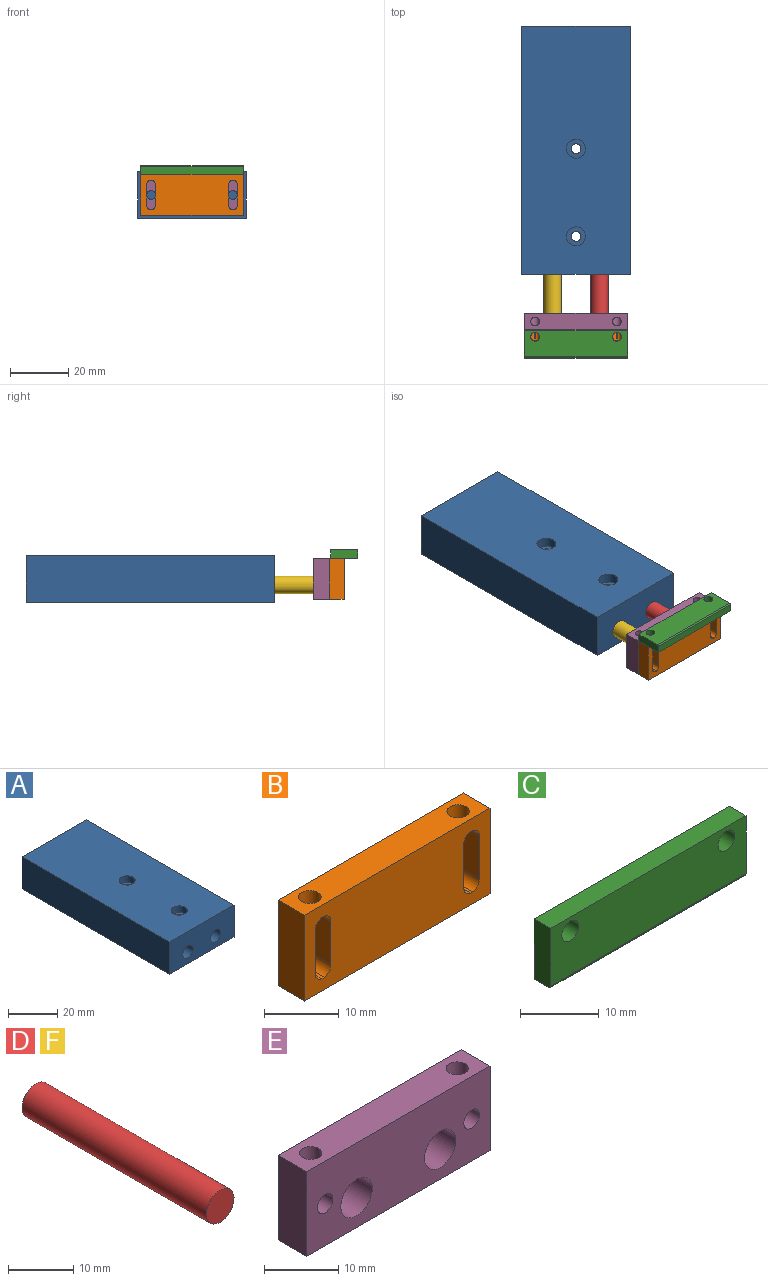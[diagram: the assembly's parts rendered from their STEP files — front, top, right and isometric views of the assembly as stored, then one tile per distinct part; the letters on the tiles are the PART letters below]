
ASSEMBLY  parts=6 mates=8
PART A: 16 faces, bbox 37x85x16 mm
  f0: plane 37x16mm, normal (0,-1,0), area 535.5mm2, adj f1,f3,f4,f5,f6,f8
  f1: plane 85x16mm, normal (1,0,0), area 1360mm2, adj f0,f2,f4,f5
  f2: plane 37x16mm, normal (0,1,0), area 592mm2, adj f1,f3,f4,f5
  f3: plane 85x16mm, normal (-1,0,0), area 1360mm2, adj f0,f2,f4,f5
  f4: plane 85x37mm, normal (0,0,1), area 3078.6mm2, adj f0,f1,f2,f3,f12,f15
  f5: plane 85x37mm, normal (0,0,-1), area 3126.8mm2, adj f0,f1,f2,f3,f10,f13
  f6: cylinder r=3mm len=80mm, axis (0,-1,0), area 1508mm2, adj f0,f7
  f7: plane 6x6mm, normal (0,-1,0), area 28.3mm2, adj f6
  f8: cylinder r=3mm len=80mm, axis (0,-1,0), area 1508mm2, adj f0,f9
  f9: plane 6x6mm, normal (0,-1,0), area 28.3mm2, adj f8
  f10: cylinder r=1.7mm len=12.7mm, axis (0,0,1), area 135.7mm2, adj f5,f11
  f11: plane 6.5x6.5mm, normal (0,0,1), area 24.1mm2, adj f10,f12
  f12: cylinder r=3.25mm len=6.5mm, axis (0,0,1), area 67.4mm2, adj f4,f11
  f13: cylinder r=1.7mm len=12.7mm, axis (0,0,1), area 135.7mm2, adj f5,f14
  f14: plane 6.5x6.5mm, normal (0,0,1), area 24.1mm2, adj f13,f15
  f15: cylinder r=3.25mm len=6.5mm, axis (0,0,1), area 67.4mm2, adj f4,f14
PART B: 30 faces, bbox 35x5x14 mm
  f0: plane 35x5mm, normal (0,0,1), area 160.9mm2, adj f10,f11,f12,f13,f28,f29
  f1: cylinder r=1.5mm len=2.5mm, axis (0,-1,0), area 3.4mm2, adj f3,f13,f16,f29
  f2: cylinder r=1.5mm len=2.5mm, axis (0,-1,0), area 3.4mm2, adj f12,f16,f17,f29
  f3: plane 1.02x0.43mm, normal (0,0,-1), area 0.4mm2, adj f1,f5,f13,f29
  f4: cylinder r=1.5mm len=2.5mm, axis (0,-1,0), area 3.4mm2, adj f12,f17,f19,f29
  f5: cylinder r=1.5mm len=2.5mm, axis (0,-1,0), area 3.4mm2, adj f3,f13,f19,f29
  f6: plane 1.02x0.43mm, normal (0,0,-1), area 0.4mm2, adj f7,f12,f25,f28
  f7: cylinder r=1.5mm len=2.5mm, axis (0,-1,0), area 3.4mm2, adj f6,f12,f22,f28
  f8: cylinder r=1.5mm len=2.5mm, axis (0,-1,0), area 3.4mm2, adj f13,f20,f27,f28
  f9: plane 35x5mm, normal (0,0,-1), area 175mm2, adj f10,f11,f12,f13
  f10: plane 14x5mm, normal (1,0,0), area 70mm2, adj f0,f9,f12,f13
  f11: plane 14x5mm, normal (-1,0,0), area 70mm2, adj f0,f9,f12,f13
  f12: plane 35x14mm, normal (0,-1,0), area 433.6mm2, adj f0,f2,f4,f6,f7,f9,f10,f11
  f13: plane 35x14mm, normal (0,1,0), area 433.6mm2, adj f0,f1,f3,f5,f8,f9,f10,f11
  f14: plane 5x0.43mm, normal (0,0,1), area 2.2mm2, adj f12,f13,f15,f18
  f15: cylinder r=1.5mm len=5mm, axis (0,-1,0), area 10.7mm2, adj f12,f13,f14,f16
  f16: plane 7.04x5mm, normal (-1,0,0), area 35.2mm2, adj f1,f2,f12,f13,f15
  f17: plane 1.02x0.43mm, normal (0,0,-1), area 0.4mm2, adj f2,f4,f12,f29
  f18: cylinder r=1.5mm len=5mm, axis (0,-1,0), area 10.7mm2, adj f12,f13,f14,f19
  f19: plane 7.04x5mm, normal (1,0,0), area 35.2mm2, adj f4,f5,f12,f13,f18
  f20: plane 1.02x0.43mm, normal (0,0,-1), area 0.4mm2, adj f8,f13,f21,f28
  f21: cylinder r=1.5mm len=2.5mm, axis (0,-1,0), area 3.4mm2, adj f13,f20,f22,f28
  f22: plane 7.04x5mm, normal (1,0,0), area 35.2mm2, adj f7,f12,f13,f21,f23
  f23: cylinder r=1.5mm len=5mm, axis (0,-1,0), area 10.7mm2, adj f12,f13,f22,f24
  f24: plane 5x0.43mm, normal (0,0,1), area 2.2mm2, adj f12,f13,f23,f26
  f25: cylinder r=1.5mm len=2.5mm, axis (0,-1,0), area 3.4mm2, adj f6,f12,f27,f28
  f26: cylinder r=1.5mm len=5mm, axis (0,-1,0), area 10.7mm2, adj f12,f13,f24,f27
  f27: plane 7.04x5mm, normal (-1,0,0), area 35.2mm2, adj f8,f12,f13,f25,f26
  f28: cylinder r=1.5mm len=3.48mm, axis (0,0,1), area 23.8mm2, adj f0,f6,f7,f8,f20,f21,f25
  f29: cylinder r=1.5mm len=3.48mm, axis (0,0,1), area 23.8mm2, adj f0,f1,f2,f3,f4,f5,f17
PART C: 9 faces, bbox 35x3x9.4 mm
  f0: plane 35x8.97mm, normal (0,-1,0), area 299.6mm2, adj f3,f4,f5,f6,f7,f8
  f1: plane 35x9.37mm, normal (0,1,0), area 313.6mm2, adj f2,f3,f4,f5,f6,f7
  f2: plane 35x2.6mm, normal (0,0,-1), area 91mm2, adj f1,f3,f5,f8
  f3: plane 9.37x3mm, normal (1,0,0), area 28.1mm2, adj f0,f1,f2,f4,f8
  f4: plane 35x3mm, normal (0,0,1), area 105mm2, adj f0,f1,f3,f5
  f5: plane 9.37x3mm, normal (-1,0,0), area 28.1mm2, adj f0,f1,f2,f4,f8
  f6: cylinder r=1.5mm len=3mm, axis (0,-1,0), area 28.3mm2, adj f0,f1
  f7: cylinder r=1.5mm len=3mm, axis (0,-1,0), area 28.3mm2, adj f0,f1
  f8: cylinder r=0.4mm len=35mm, axis (-1,0,0), area 22mm2, adj f0,f2,f3,f5
PART D: 3 faces, bbox 6x40x6 mm
  f0: cylinder r=3mm len=40mm, axis (0,1,0), area 754mm2, adj f1,f2
  f1: plane 6x6mm, normal (0,-1,0), area 28.3mm2, adj f0
  f2: plane 6x6mm, normal (0,1,0), area 28.3mm2, adj f0
PART E: 12 faces, bbox 35x5.5x14 mm
  f0: plane 35x5.5mm, normal (0,0,1), area 178.4mm2, adj f2,f3,f5,f8,f10,f11
  f1: cylinder r=1.5mm len=5.5mm, axis (0,-1,0), area 42.8mm2, adj f2,f3,f10
  f2: plane 35x14mm, normal (0,-1,0), area 419.3mm2, adj f0,f1,f4,f5,f6,f7,f8,f9
  f3: plane 35x14mm, normal (0,1,0), area 419.3mm2, adj f0,f1,f4,f5,f6,f7,f8,f9
  f4: plane 35x5.5mm, normal (0,0,-1), area 192.5mm2, adj f2,f3,f5,f8
  f5: plane 14x5.5mm, normal (1,0,0), area 77mm2, adj f0,f2,f3,f4
  f6: cylinder r=3mm len=6mm, axis (0,1,0), area 103.7mm2, adj f2,f3
  f7: cylinder r=3mm len=6mm, axis (0,1,0), area 103.7mm2, adj f2,f3
  f8: plane 14x5.5mm, normal (-1,0,0), area 77mm2, adj f0,f2,f3,f4
  f9: cylinder r=1.5mm len=5.5mm, axis (0,-1,0), area 42.8mm2, adj f2,f3,f11
  f10: cylinder r=1.5mm len=7mm, axis (0,0,1), area 57mm2, adj f0,f1
  f11: cylinder r=1.5mm len=7mm, axis (0,0,1), area 57mm2, adj f0,f9
PART F: same geometry as D
PLACE A t=(-142.29,71.57,-80.13)mm
PLACE B t=(-142.29,10.21,-72.13)mm
PLACE C rot(axis=(-1,0,0),90deg) t=(-142.29,5.46,-65.13)mm
PLACE D t=(-134.29,50.21,-74.13)mm
PLACE E t=(-142.29,15.71,-72.13)mm
PLACE F t=(-150.29,50.21,-74.13)mm
MATE slider D.f0 <-> A.f6  axis (0,1,0) through (-134.29,30.21,-74.13)mm
MATE fastened D.f0 <-> E.f6  axis (0,-1,0) through (-134.29,10.21,-74.13)mm
MATE slider D.f0 <-> A.f6  axis (0,1,0) through (-134.29,30.21,-74.13)mm
MATE slider A.f6 <-> A.f8  axis (0,-1,0) through (-134.29,29.07,-74.13)mm
MATE fastened E.f7 <-> F.f0  axis (0,-1,0) through (-150.29,10.21,-74.13)mm
MATE fastened C.f6 <-> B.f29  axis (0,0,-1) through (-128.29,7.71,-65.13)mm
MATE fastened B.f13 <-> E.f2  axis (0,1,0) through (-124.79,10.21,-79.13)mm
MATE slider F.f0 <-> A.f8  axis (0,1,0) through (-150.29,30.21,-74.13)mm
